# Revit family: Pump_Commercial-Submersible-Zoeller-63_Automatic_Series
name_source: partatom
category: Mechanical Equipment
revit_build: Autodesk Revit 2014 (Build: 20130308_1515(x64)
units: mm (PartAtom-declared; Revit-internal decimal feet)

## types (1)
- M63 115V 1Ph
    Amps = 10 A
    Apparent Load = 1116 VA
    Assembly Code = D2010900
    Cooling = Oil Filled
    Cord Length = 120"
    Cord Type = UL listed, 3-wire, grounded plug
    Default Elevation = 7 7/8"
    Description = PREMIUM SERIES submersible pump for dewatering (sump) systems
    Discharge Diameter = 1 1/2" NPT
    Discharge Height = 3 3/32"
    Discharge Radius = 3/4"
    Height = 10 1/16"
    Hertz = 60
    Impeller = Engineered Thermoplastic
    Impeller Type = Non-clogging vortex
    Installation Type = Floor Mounted
    Insulation = Class B
    Lead Wires Insulation = Class B
    Length = 7 7/8"
    Lower Bearing = Sleeve Bearing
    Manufacturer = Zoeller
    Material = Cast Iron-Zoeller-Powder Coated Epoxy
    Max Flow @ 5' = 43 GPM
    Max. Water Temp. = 130 °F
    Maximum Head = 19 1/4 ft
    Model = M63
    Motor = 3/10 HP
    Motor Protection = Auto Reset Thermal Overload.
    Motor Type = Submersible
    O-Rings and Cover Gasket = Neoprene
    Off Point = 3"
    On Point = 7 1/4"
    Operation = Automatic
    Phase = 1
    Price = Prices may vary. Please consult Manufacturer Representative for most up-to-date price list.
    Product Page URL = http://www.zoellerpumps.com
    RPM = 1550
    Shaft Seal = Carbon/Ceramic
    Solid Handling = 1/2" Spherical Solids
    Type = Shaded Pole Motor
    Type Comments = Automatic or Non-Automatic available
    URL = http://www.zoellerengprod.com
    Upper Bearing = Sleeve Bearing
    Voltage = 115 V
    Warranty Information = 36 Months (Limited)
    Waste Connection = Yes
    Width = 10 3/32"

## geometry (parser evidence)
native form markers: Sweep x2
no freeform markers — native parametric forms only
